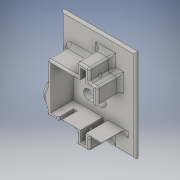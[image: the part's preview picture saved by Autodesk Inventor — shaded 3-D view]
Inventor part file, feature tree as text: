
AUTODESK INVENTOR PART (.ipt)
format: ipt  version: 2016 (Build 200138000, 138)  size: 625,152 bytes
history: native  units: in
note: dims shown in document units (in); Inventor stores cm internally (conversion verified against a paired STEP export)
features: sketch x10, other x3
ambient origin geometry x8: Origin, YZ Plane, XZ Plane, XY Plane, X Axis, Y Axis, Z Axis, Center Point
bodies: Solid1 (feature_tree)
feature tree (13):
  other  "sole_v1.ipt"
  other  "Solid1::sole_v1.ipt"
  other  "TaggingFeature1"
  sketch  "Sketch1"  dims[d0=0.3937in]
  sketch  "Sketch12"
  sketch  "Sketch14"
  sketch  "Sketch17"
  sketch  "Sketch18"
  sketch  "Sketch20"
  sketch  "Sketch21"
  sketch  "Sketch22"
  sketch  "Sketch23"
  sketch  "Sketch24"
